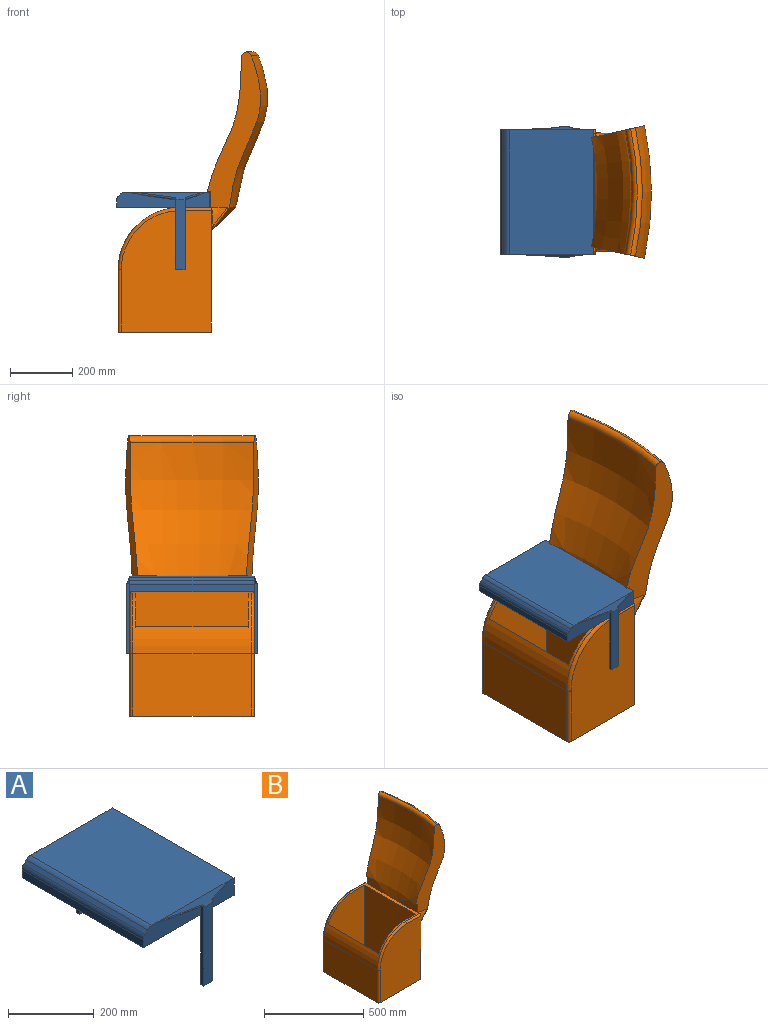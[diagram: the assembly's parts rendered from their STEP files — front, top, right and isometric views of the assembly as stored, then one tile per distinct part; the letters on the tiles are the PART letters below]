
ASSEMBLY  parts=2 mates=1
PART A: 31 faces, bbox 301.2x423.1x256.8 mm
  f0: plane 80x50mm, normal (0,-1,0), area 3110.5mm2, adj f3,f4,f5,f7,f12,f14
  f1: plane 190x50mm, normal (0,-1,0), area 7153.2mm2, adj f2,f3,f5,f8,f13,f15,f28,f29
  f2: plane 400x21.72mm, normal (-1,0,0), area 8686.3mm2, adj f1,f3,f17,f30
  f3: plane 400x300mm, normal (0,0,-1), area 120000mm2, adj f0,f1,f2,f4,f6,f16,f17,f18
  f4: plane 400x50mm, normal (1,0,0), area 20000mm2, adj f0,f3,f5,f16
  f5: plane 400x271.72mm, normal (0,0,1), area 108686.3mm2, adj f0,f1,f4,f11,f16,f17,f23,f29
  f6: plane 199.8x30mm, normal (0,1,0), area 5993.8mm2, adj f3,f7,f8,f9
  f7: plane 233.34x11.23mm, normal (1,0,0), area 2262.7mm2, adj f0,f6,f9,f10,f11,f12,f14
  f8: plane 232.3x10.57mm, normal (-1,0,0), area 2260.4mm2, adj f1,f6,f9,f10,f11,f13,f15
  f9: plane 30x10mm, normal (0,0,-1), area 300mm2, adj f6,f7,f8,f10
  f10: plane 225.61x30.01mm, normal (0,-1,0), area 6757.2mm2, adj f7,f8,f9,f11
  f11: bspline ~300x25mm, area 2682.6mm2, adj f5,f7,f8,f10,f14,f15
  f12: plane 21.77x6.75mm, normal (0.3,0,-0.96), area 31.5mm2, adj f0,f7,f14
  f13: plane 51.71x6.8mm, normal (-0.13,0,-0.99), area 73.3mm2, adj f1,f8,f15
  f14: bspline ~86.81x32.85mm, area 496.6mm2, adj f0,f7,f11,f12
  f15: bspline ~178.84x30.24mm, area 1150.2mm2, adj f1,f8,f11,f13
  f16: plane 80x50mm, normal (0,1,0), area 3110.5mm2, adj f3,f4,f5,f19,f24,f26
  f17: plane 190x50mm, normal (0,1,0), area 7153.2mm2, adj f2,f3,f5,f20,f25,f27,f28,f29
  f18: plane 199.8x30mm, normal (0,-1,0), area 5993.8mm2, adj f3,f19,f20,f21
  f19: plane 233.34x11.23mm, normal (1,0,0), area 2262.7mm2, adj f16,f18,f21,f22,f23,f24,f26
  f20: plane 232.3x10.57mm, normal (-1,0,0), area 2260.4mm2, adj f17,f18,f21,f22,f23,f25,f27
  f21: plane 30x10mm, normal (0,0,-1), area 300mm2, adj f18,f19,f20,f22
  f22: plane 225.61x30.01mm, normal (0,1,0), area 6757.2mm2, adj f19,f20,f21,f23
  f23: bspline ~300x25mm, area 2682.6mm2, adj f5,f19,f20,f22,f26,f27
  f24: plane 21.77x6.75mm, normal (0.3,0,-0.96), area 31.5mm2, adj f16,f19,f26
  f25: plane 51.71x6.8mm, normal (-0.13,0,-0.99), area 73.3mm2, adj f17,f20,f27
  f26: bspline ~86.81x32.85mm, area 496.6mm2, adj f16,f19,f23,f24
  f27: bspline ~178.84x30.24mm, area 1150.2mm2, adj f17,f20,f23,f25
  f28: plane 400x8.28mm, normal (-0.71,0,0.71), area 4686.3mm2, adj f1,f17,f29,f30
  f29: cylinder r=20mm len=400mm, axis (0,-1,0), area 6283.2mm2, adj f1,f5,f17,f28
  f30: cylinder r=20mm len=400mm, axis (0,-1,0), area 6283.2mm2, adj f1,f2,f17,f28
PART B: 41 faces, bbox 567.2x467.4x920 mm
  f0: revolved ~479.94x398.32mm, area 177889.5mm2, adj f2,f4,f5,f6,f7,f8,f27
  f1: plane 357.7x3.95mm, normal (0,0,-1), area 1410.4mm2, adj f2,f4,f9,f24
  f2: plane 535.6x192.13mm, normal (-0.22,-0.98,0), area 33565.2mm2, adj f0,f1,f3,f7,f8,f10,f21,f22
  f3: revolved ~480.24x425.76mm, area 206500.8mm2, adj f2,f4,f25,f26
  f4: plane 536.17x192.11mm, normal (-0.22,0.98,0), area 33565.8mm2, adj f0,f1,f3,f5,f6,f10,f22,f23
  f5: plane 58.58x10.4mm, normal (0,0,-1), area 285.4mm2, adj f0,f4,f6
  f6: plane 197.39x72.02mm, normal (-1,0,0), area 5382.8mm2, adj f0,f4,f5,f10
  f7: plane 197.38x72.02mm, normal (-1,0,0), area 5382.8mm2, adj f0,f2,f8,f10
  f8: plane 58.58x10.4mm, normal (0,0,-1), area 285.4mm2, adj f0,f2,f7
  f9: plane 400x400mm, normal (1,0,0), area 131643.9mm2, adj f1,f10,f12,f14,f15,f24,f30,f33
  f10: plane 380x100mm, normal (0,0,1), area 8210.3mm2, adj f2,f4,f6,f7,f9,f11,f16,f17
  f11: cylinder r=200mm len=380mm, axis (0,1,0), area 38757.1mm2, adj f10,f13,f16,f17,f18,f29,f32
  f12: plane 400x300mm, normal (0,0,-1), area 119957.1mm2, adj f9,f13,f14,f15,f28,f31
  f13: plane 380x200mm, normal (-1,0,0), area 76000mm2, adj f11,f12,f28,f31
  f14: plane 390x290mm, normal (0,-1,0), area 105352.9mm2, adj f9,f12,f31,f32,f33
  f15: plane 390x290mm, normal (0,1,0), area 105352.9mm2, adj f9,f12,f28,f29,f30
  f16: plane 380x260mm, normal (0,1,0), area 93041.4mm2, adj f10,f11,f18,f19,f20
  f17: plane 380x260mm, normal (0,-1,0), area 93041.4mm2, adj f10,f11,f18,f19,f20
  f18: plane 360x267.18mm, normal (1,0,0), area 96184.1mm2, adj f11,f16,f17,f20
  f19: plane 380x360mm, normal (-1,0,0), area 136800mm2, adj f10,f16,f17,f20
  f20: plane 360x260mm, normal (0,0,1), area 93600mm2, adj f16,f17,f18,f19
  f21: bspline ~73.84x58.05mm, area 1611.6mm2, adj f2,f24,f34,f35
  f22: bspline ~381.75x78.95mm, area 34938.7mm2, adj f2,f4,f25,f35,f37,f38
  f23: bspline ~73.84x58.05mm, area 1605.7mm2, adj f4,f24,f38,f40
  f24: plane 383.43x4.08mm, normal (-0.6,0,0.8), area 1834.8mm2, adj f1,f9,f21,f23,f34,f40
  f25: bspline ~387.15x26.83mm, area 6331.5mm2, adj f2,f3,f4,f22
  f26: torus R=934.85mm, axis (0,0,-1), area 8834.9mm2, adj f2,f3,f4,f27
  f27: torus R=940.16mm, axis (0,0,-1), area 11644.3mm2, adj f0,f2,f4,f26
  f28: cylinder r=10mm len=200mm, axis (0,0,-1), area 3141.6mm2, adj f12,f13,f15,f29
  f29: torus R=190mm, axis (0,-1,0), area 4845.1mm2, adj f11,f15,f28,f30
  f30: cylinder r=10mm len=100mm, axis (-1,0,0), area 1570.8mm2, adj f9,f10,f15,f29
  f31: cylinder r=10mm len=200mm, axis (0,0,1), area 3141.6mm2, adj f12,f13,f14,f32
  f32: torus R=190mm, axis (0,-1,0), area 4845.1mm2, adj f11,f14,f31,f33
  f33: cylinder r=10mm len=100mm, axis (1,0,0), area 1570.8mm2, adj f9,f10,f14,f32
  f34: bspline ~61.68x6.83mm, area 368.8mm2, adj f9,f21,f24,f36
  f35: bspline ~92.38x74.3mm, area 515mm2, adj f2,f21,f22,f36
  f36: bspline ~17.96x11.42mm, area 93.8mm2, adj f9,f34,f35,f37
  f37: bspline ~401.09x3.65mm, area 1437.5mm2, adj f9,f22,f36,f39
  f38: bspline ~92.18x74.17mm, area 512.1mm2, adj f4,f22,f23,f39
  f39: bspline ~18.98x10.62mm, area 94.4mm2, adj f9,f37,f38,f40
  f40: bspline ~61.19x6.85mm, area 371.3mm2, adj f9,f23,f24,f39
PLACE A rot(axis=(0,-1,-0.01),0deg) t=(-36.71,-23.46,26.25)mm
PLACE B t=(277.41,-23.46,43.35)mm fixed
MATE revolute A.f6 <-> B.f11  axis (0,1,0) through (180.2,-223.46,-156.65)mm
